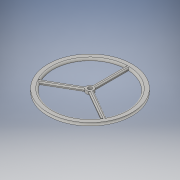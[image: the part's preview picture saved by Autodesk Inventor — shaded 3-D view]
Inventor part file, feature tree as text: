
AUTODESK INVENTOR PART (.ipt)
format: ipt  version: 2016 (Build 200138000, 138)  size: 258,560 bytes
history: native  units: in
note: dims shown in document units (in); Inventor stores cm internally (conversion verified against a paired STEP export)
features: fillet x5, sketch x2, revolve x1, extrude x1
ambient origin geometry x8: Origin, YZ Plane, XZ Plane, XY Plane, X Axis, Y Axis, Z Axis, Center Point
bodies: Solid1 (feature_tree)
feature tree (9):
  revolve  "Revolution1"  [1 undecoded]
  extrude  "Extrusion1"  Depth=0.05in
  fillet  "Fillet1"  Radius=0.105in
  fillet  "Fillet4"  Radius=0.1in
  fillet  "Fillet5"  Radius=0.1in
  fillet  "Fillet6"  Radius=0.05in
  fillet  "Fillet7"  [1 undecoded]
  sketch  "Sketch1"  dims[d5=90.0deg d14=1.0in d15=0.0in]
  sketch  "Sketch2"  dims[d16=0.06in d19=0.06in d22=0.105in d24=0.1in d25=0.1in d26=0.05in]
note: 2 required parameter values undecoded (feature->parameter linkage not recoverable at this tier; creation-order binding heuristic only, values carry confidence <= 0.55)